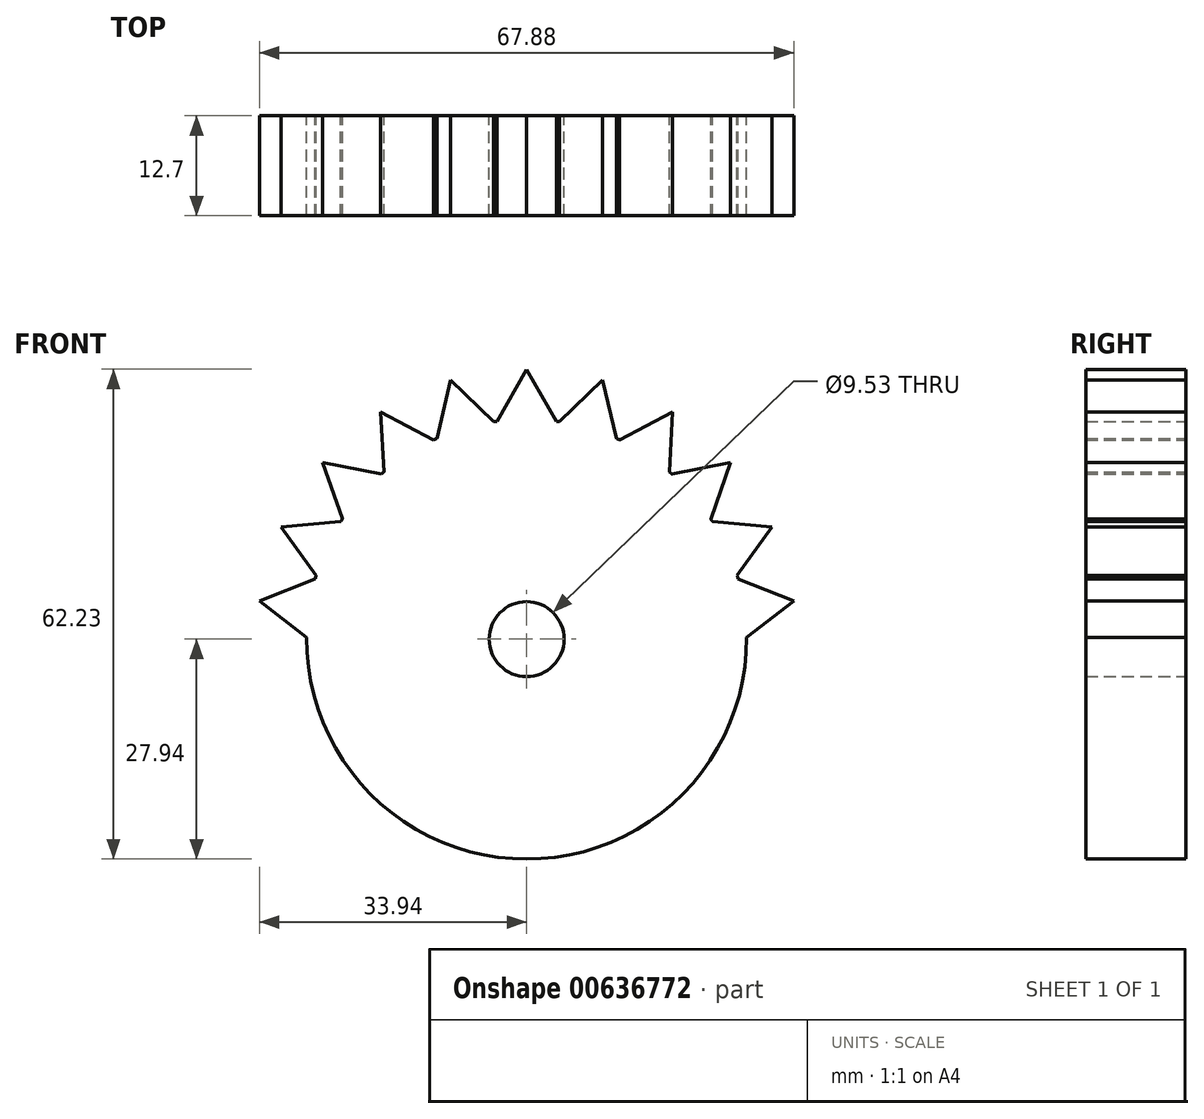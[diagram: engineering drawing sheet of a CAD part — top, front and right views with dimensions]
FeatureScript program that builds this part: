
annotation { "Feature Type Name" : "Feature", "Feature Type Description" : "" }
export const myFeature = defineFeature(function(context is Context, id is Id, definition is map)
    precondition{}
    {
        {
            var Q0;
            Q0=qCreatedBy(makeId("Front.planeOp"),FACE);
            var sketch = newSketch(context, id + "F0", { "sketchPlane" : qUnion([Q0])});
            skCircle(sketch, "E0", {"center": v(0, 0) * mm, "radius": 27.94 * mm});
            skLineSegment(sketch, "E1", {"start": v(0, 34.29) * mm, "end": v(0, 27.94) * mm, "construction": true});
            skLineSegment(sketch, "E2", {"start": v(0, 34.29) * mm, "end": v(-3.76, 27.68) * mm});
            skLineSegment(sketch, "E3.MirrorCS", {"start": v(0, 34.29) * mm, "end": v(3.76, 27.68) * mm});
            skLineSegment(sketch, "E4.1.0", {"start": v(-9.66, 32.9) * mm, "end": v(-11.41, 25.5) * mm});
            skLineSegment(sketch, "E4.1.1", {"start": v(-9.66, 32.9) * mm, "end": v(-4.19, 27.62) * mm});
            skLineSegment(sketch, "E4.2.0", {"start": v(-18.54, 28.84) * mm, "end": v(-18.13, 21.25) * mm});
            skLineSegment(sketch, "E4.2.1", {"start": v(-18.54, 28.84) * mm, "end": v(-11.8, 25.32) * mm});
            skLineSegment(sketch, "E4.3.0", {"start": v(-25.91, 22.45) * mm, "end": v(-23.39, 15.28) * mm});
            skLineSegment(sketch, "E4.3.1", {"start": v(-25.91, 22.45) * mm, "end": v(-18.46, 20.97) * mm});
            skLineSegment(sketch, "E4.4.0", {"start": v(-31.19, 14.24) * mm, "end": v(-26.74, 8.08) * mm});
            skLineSegment(sketch, "E4.4.1", {"start": v(-31.19, 14.24) * mm, "end": v(-23.62, 14.92) * mm});
            skLineSegment(sketch, "E4.5.0", {"start": v(-33.94, 4.88) * mm, "end": v(-27.94, 0.21) * mm});
            skLineSegment(sketch, "E4.5.1", {"start": v(-33.94, 4.88) * mm, "end": v(-26.87, 7.67) * mm});
            skLineSegment(sketch, "E4.17.0", {"start": v(33.94, 4.88) * mm, "end": v(26.87, 7.67) * mm});
            skLineSegment(sketch, "E4.17.1", {"start": v(33.94, 4.88) * mm, "end": v(27.94, 0.21) * mm});
            skLineSegment(sketch, "E4.18.0", {"start": v(31.19, 14.24) * mm, "end": v(23.62, 14.92) * mm});
            skLineSegment(sketch, "E4.18.1", {"start": v(31.19, 14.24) * mm, "end": v(26.74, 8.08) * mm});
            skLineSegment(sketch, "E4.19.0", {"start": v(25.91, 22.45) * mm, "end": v(18.46, 20.97) * mm});
            skLineSegment(sketch, "E4.19.1", {"start": v(25.91, 22.45) * mm, "end": v(23.39, 15.28) * mm});
            skLineSegment(sketch, "E4.20.0", {"start": v(18.54, 28.84) * mm, "end": v(11.8, 25.32) * mm});
            skLineSegment(sketch, "E4.20.1", {"start": v(18.54, 28.84) * mm, "end": v(18.13, 21.25) * mm});
            skLineSegment(sketch, "E4.21.0", {"start": v(9.66, 32.9) * mm, "end": v(4.19, 27.62) * mm});
            skLineSegment(sketch, "E4.21.1", {"start": v(9.66, 32.9) * mm, "end": v(11.41, 25.5) * mm});
            skSolve(sketch);
        }
        {
            var Q0;
            {var subQ0=sQuery(id+"F0.wireOp",EDGE,"E4.17.0");Q0=makeQuery(id+"F0.imprint","IMPRINT",FACE,{"disambiguationData":[TD([[makeQuery(id+"F0.imprint","IMPRINT",EDGE,{"derivedFrom":subQ0}),1.0]])]});}
            var Q1;
            {var subQ0=sQuery(id+"F0.wireOp",EDGE,"E4.18.0");Q1=makeQuery(id+"F0.imprint","IMPRINT",FACE,{"disambiguationData":[TD([[makeQuery(id+"F0.imprint","IMPRINT",EDGE,{"derivedFrom":subQ0}),1.0]])]});}
            var Q2;
            {var subQ0=sQuery(id+"F0.wireOp",EDGE,"E4.19.0");Q2=makeQuery(id+"F0.imprint","IMPRINT",FACE,{"disambiguationData":[TD([[makeQuery(id+"F0.imprint","IMPRINT",EDGE,{"derivedFrom":subQ0}),1.0]])]});}
            var Q3;
            {var subQ0=sQuery(id+"F0.wireOp",EDGE,"E4.20.0");Q3=makeQuery(id+"F0.imprint","IMPRINT",FACE,{"disambiguationData":[TD([[makeQuery(id+"F0.imprint","IMPRINT",EDGE,{"derivedFrom":subQ0}),1.0]])]});}
            var Q4;
            {var subQ0=sQuery(id+"F0.wireOp",EDGE,"E0");var subQ8=makeQuery(id+"F0.imprint","INTERSECT",VERTEX,{"derivedFrom":[subQ0,sQuery(id+"F0.wireOp",EDGE,"E4.17.0")]});Q4=makeQuery(id+"F0.imprint","IMPRINT",FACE,{"disambiguationData":[TD([[makeQuery(id+"F0.imprint","IMPRINT",EDGE,{"disambiguationData":[TD([[subQ8,1.0]])],"derivedFrom":subQ0}),1.0]])]});}
            var Q5;
            {var subQ0=sQuery(id+"F0.wireOp",EDGE,"E4.21.0");Q5=makeQuery(id+"F0.imprint","IMPRINT",FACE,{"disambiguationData":[TD([[makeQuery(id+"F0.imprint","IMPRINT",EDGE,{"derivedFrom":subQ0}),1.0]])]});}
            var Q6;
            {var subQ0=sQuery(id+"F0.wireOp",EDGE,"E2");Q6=makeQuery(id+"F0.imprint","IMPRINT",FACE,{"disambiguationData":[TD([[makeQuery(id+"F0.imprint","IMPRINT",EDGE,{"derivedFrom":subQ0}),1.0]])]});}
            var Q7;
            {var subQ0=sQuery(id+"F0.wireOp",EDGE,"E4.1.0");Q7=makeQuery(id+"F0.imprint","IMPRINT",FACE,{"disambiguationData":[TD([[makeQuery(id+"F0.imprint","IMPRINT",EDGE,{"derivedFrom":subQ0}),1.0]])]});}
            var Q8;
            {var subQ0=sQuery(id+"F0.wireOp",EDGE,"E4.2.0");Q8=makeQuery(id+"F0.imprint","IMPRINT",FACE,{"disambiguationData":[TD([[makeQuery(id+"F0.imprint","IMPRINT",EDGE,{"derivedFrom":subQ0}),1.0]])]});}
            var Q9;
            {var subQ0=sQuery(id+"F0.wireOp",EDGE,"E4.3.0");Q9=makeQuery(id+"F0.imprint","IMPRINT",FACE,{"disambiguationData":[TD([[makeQuery(id+"F0.imprint","IMPRINT",EDGE,{"derivedFrom":subQ0}),1.0]])]});}
            var Q10;
            {var subQ0=sQuery(id+"F0.wireOp",EDGE,"E4.4.0");Q10=makeQuery(id+"F0.imprint","IMPRINT",FACE,{"disambiguationData":[TD([[makeQuery(id+"F0.imprint","IMPRINT",EDGE,{"derivedFrom":subQ0}),1.0]])]});}
            var Q11;
            {var subQ0=sQuery(id+"F0.wireOp",EDGE,"E4.5.0");Q11=makeQuery(id+"F0.imprint","IMPRINT",FACE,{"disambiguationData":[TD([[makeQuery(id+"F0.imprint","IMPRINT",EDGE,{"derivedFrom":subQ0}),1.0]])]});}
            extrude(context, id + "F1", {"entities" : qUnion([Q0, Q1, Q2, Q3, Q4, Q5, Q6, Q7, Q8, Q9, Q10, Q11]), "depth" : 12.7 * mm, "offsetDistance" : 25.4 * mm});
        }
        {
            var Q0;
            {var subQ0=sQuery(id+"F0.wireOp",EDGE,"E0");var subQ8=makeQuery(id+"F0.imprint","INTERSECT",VERTEX,{"derivedFrom":[subQ0,sQuery(id+"F0.wireOp",EDGE,"E4.17.0")]});Q0=makeQuery(id+"F0.imprint","IMPRINT",FACE,{"disambiguationData":[TD([[makeQuery(id+"F0.imprint","IMPRINT",EDGE,{"disambiguationData":[TD([[subQ8,1.0]])],"derivedFrom":subQ0}),1.0]])]});}
            var sketch = newSketch(context, id + "F2", { "sketchPlane" : qUnion([Q0])});
            skCircle(sketch, "E5", {"center": v(0, 0) * mm, "radius": 4.76 * mm});
            skSolve(sketch);
        }
        {
            var Q0;
            Q0=makeQuery(id+"F2.imprint","IMPRINT",FACE,{"disambiguationData":[TD([[makeQuery(id+"F2.imprint","IMPRINT",EDGE,{"derivedFrom":sQuery(id+"F2.wireOp",EDGE,"E5")}),1.0]])]});
            extrude(context, id + "F3", {"entities" : qUnion([Q0]), "operationType" : NewBodyOperationType.REMOVE, "depth" : 12.7 * mm, "offsetDistance" : 25.4 * mm});
        }
    });
